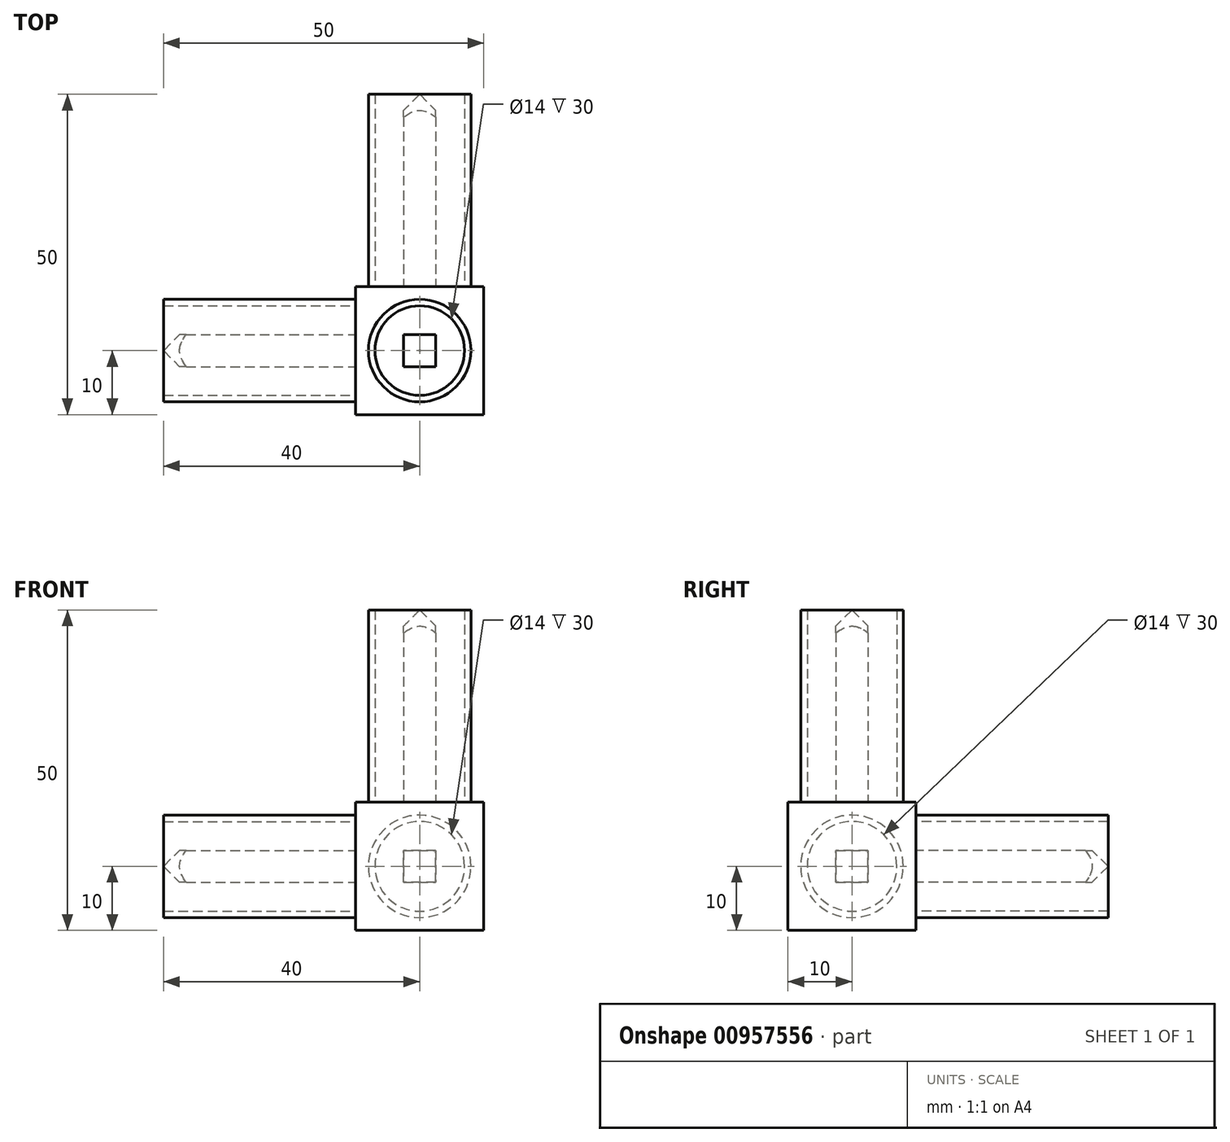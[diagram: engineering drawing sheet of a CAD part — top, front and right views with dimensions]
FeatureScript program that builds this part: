
annotation { "Feature Type Name" : "Feature", "Feature Type Description" : "" }
export const myFeature = defineFeature(function(context is Context, id is Id, definition is map)
    precondition{}
    {
        {
            var Q0;
            Q0=qCreatedBy(makeId("Top.planeOp"),FACE);
            var sketch = newSketch(context, id + "F0", { "sketchPlane" : qUnion([Q0])});
            skLineSegment(sketch, "E0.bottom", {"start": v(10, 10) * mm, "end": v(-10, 10) * mm});
            skLineSegment(sketch, "E0.top", {"start": v(10, -10) * mm, "end": v(-10, -10) * mm});
            skLineSegment(sketch, "E0.left", {"start": v(10, 10) * mm, "end": v(10, -10) * mm});
            skLineSegment(sketch, "E0.right", {"start": v(-10, 10) * mm, "end": v(-10, -10) * mm});
            skPoint(sketch, "E0.middle", {"position": v(0, 0) * mm});
            skSolve(sketch);
        }
        {
            var Q0;
            Q0 = qSketchRegion(id + "F0", true);
            extrude(context, id + "F1", {"entities" : qUnion([Q0]), "oppositeDirection" : true, "depth" : 10 * mm, "offsetDistance" : 25.4 * mm, "hasSecondDirection" : true, "secondDirectionOppositeDirection" : false, "secondDirectionDepth" : 10 * mm});
        }
        {
            var Q0;
            Q0=makeQuery(id+"F1.opExtrude","CAP_FACE",FACE,{"disambiguationData":[OSD([sQuery(id+"F0.wireOp",EDGE,"E0.bottom"),sQuery(id+"F0.wireOp",EDGE,"E0.top"),sQuery(id+"F0.wireOp",EDGE,"E0.left"),sQuery(id+"F0.wireOp",EDGE,"E0.right")])],"isStart":true});
            var sketch = newSketch(context, id + "F2", { "sketchPlane" : qUnion([Q0])});
            skCircle(sketch, "E1", {"center": v(0, 0) * mm, "radius": 8 * mm});
            skCircle(sketch, "E2", {"center": v(0, 0) * mm, "radius": 7 * mm});
            skSolve(sketch);
        }
        {
            var Q0;
            Q0 = qSketchRegion(id + "F2", true);
            extrude(context, id + "F3", {"entities" : qUnion([Q0]), "operationType" : NewBodyOperationType.ADD, "depth" : 30 * mm, "offsetDistance" : 25.4 * mm});
        }
        {
            var Q0;
            {var subQ0=sQuery(id+"F0.wireOp",EDGE,"E0.left");var subQ1=sQuery(id+"F0.wireOp",EDGE,"E0.top");var subQ2=sQuery(id+"F0.wireOp",EDGE,"E0.right");var subQ3=sQuery(id+"F0.wireOp",EDGE,"E0.bottom");Q0=makeQuery(id+"F3.boolean.opBoolean","SPLIT",FACE,{"disambiguationData":[TD([makeQuery(id+"F1.opExtrude","SWEPT_FACE",FACE,{"disambiguationData":[OSD([subQ3])]})])],"derivedFrom":makeQuery(id+"F1.opExtrude","CAP_FACE",FACE,{"disambiguationData":[OSD([subQ3,subQ1,subQ0,subQ2])],"isStart":true})});}
            var sketch = newSketch(context, id + "F4", { "sketchPlane" : qUnion([Q0])});
            skLineSegment(sketch, "E3.bottom", {"start": v(2.5, 2.5) * mm, "end": v(-2.5, 2.5) * mm});
            skLineSegment(sketch, "E3.top", {"start": v(2.5, -2.5) * mm, "end": v(-2.5, -2.5) * mm});
            skLineSegment(sketch, "E3.left", {"start": v(2.5, 2.5) * mm, "end": v(2.5, -2.5) * mm});
            skLineSegment(sketch, "E3.right", {"start": v(-2.5, 2.5) * mm, "end": v(-2.5, -2.5) * mm});
            skPoint(sketch, "E3.middle", {"position": v(0, 0) * mm});
            skSolve(sketch);
        }
        {
            var Q0;
            Q0 = qSketchRegion(id + "F4", true);
            extrude(context, id + "F5", {"entities" : qUnion([Q0]), "operationType" : NewBodyOperationType.ADD, "depth" : 30 * mm, "offsetDistance" : 25.4 * mm});
        }
        {
            var Q0;
            Q0=qCreatedBy(makeId("Front.planeOp"),FACE);
            var sketch = newSketch(context, id + "F6", { "sketchPlane" : qUnion([Q0])});
            skLineSegment(sketch, "E4", {"start": v(0.04, 39.96) * mm, "end": v(6.35, 33.65) * mm});
            skLineSegment(sketch, "E5", {"start": v(6.35, 33.65) * mm, "end": v(6.35, 40) * mm});
            skLineSegment(sketch, "E6", {"start": v(6.35, 40) * mm, "end": v(0, 40) * mm});
            skLineSegment(sketch, "E7", {"start": v(0, 40) * mm, "end": v(0, 36.23) * mm, "construction": true});
            skPoint(sketch, "E8.visualSharp", {"position": v(0, 40) * mm});
            skLineSegment(sketch, "E9", {"start": v(0, 40) * mm, "end": v(0, 40) * mm});
            skLineSegment(sketch, "E10", {"start": v(0, 39.98) * mm, "end": v(0.04, 39.96) * mm});
            skLineSegment(sketch, "E11", {"start": v(0, 39.98) * mm, "end": v(0, 40) * mm});
            skSolve(sketch);
        }
        {
            var Q0;
            Q0=makeQuery(id+"F6.imprint","IMPRINT",FACE,{"disambiguationData":[TD([[makeQuery(id+"F6.imprint","IMPRINT",EDGE,{"derivedFrom":sQuery(id+"F6.wireOp",EDGE,"E4")}),1.0]])]});
            var Q1;
            Q1=sQuery(id+"F6.wireOp",EDGE,"E7");
            revolve(context, id + "F7", {"operationType" : NewBodyOperationType.REMOVE, "surfaceOperationType" : NewSurfaceOperationType.NEW, "entities" : qUnion([Q0]), "axis" : qUnion([Q1]), "revolveType" : RevolveType.FULL, "oppositeDirection" : true});
        }
        {
            var Q0;
            Q0=qCreatedBy(makeId("Front.planeOp"),FACE);
            var sketch = newSketch(context, id + "F8", { "sketchPlane" : qUnion([Q0])});
            skLineSegment(sketch, "E12", {"start": v(0, 0) * mm, "end": v(15.82, 0) * mm});
            skSolve(sketch);
        }
        {
            var Q0;
            Q0=makeQuery(id+"F1.opExtrude","SWEPT_BODY",BODY,{"disambiguationData":[OSD([sQuery(id+"F0.wireOp",EDGE,"E0.bottom"),sQuery(id+"F0.wireOp",EDGE,"E0.top"),sQuery(id+"F0.wireOp",EDGE,"E0.left"),sQuery(id+"F0.wireOp",EDGE,"E0.right")])]});
            var Q1;
            Q1=sQuery(id+"F8.wireOp",EDGE,"E12");
            circularPattern(context, id + "F9", {"entities" : qUnion([Q0]), "axis" : qUnion([Q1]), "angle" : 90 * degree, "instanceCount" : 2, "oppositeDirection" : true, "equalSpace" : true});
        }
        {
            var Q0;
            Q0=makeQuery(id+"F1.opExtrude","SWEPT_BODY",BODY,{"disambiguationData":[OSD([sQuery(id+"F0.wireOp",EDGE,"E0.bottom"),sQuery(id+"F0.wireOp",EDGE,"E0.top"),sQuery(id+"F0.wireOp",EDGE,"E0.left"),sQuery(id+"F0.wireOp",EDGE,"E0.right")])]});
            var Q1;
            Q1=makeQuery(id+"F9.opPattern","COPY",FACE,{"derivedFrom":makeQuery(id+"F3.opExtrude","SWEPT_FACE",FACE,{"disambiguationData":[OSD([sQuery(id+"F2.wireOp",EDGE,"E1")])]}),"instanceName":"1"});
            circularPattern(context, id + "F10", {"entities" : qUnion([Q0]), "axis" : qUnion([Q1]), "angle" : 90 * degree, "instanceCount" : 2, "equalSpace" : true});
        }
    });
